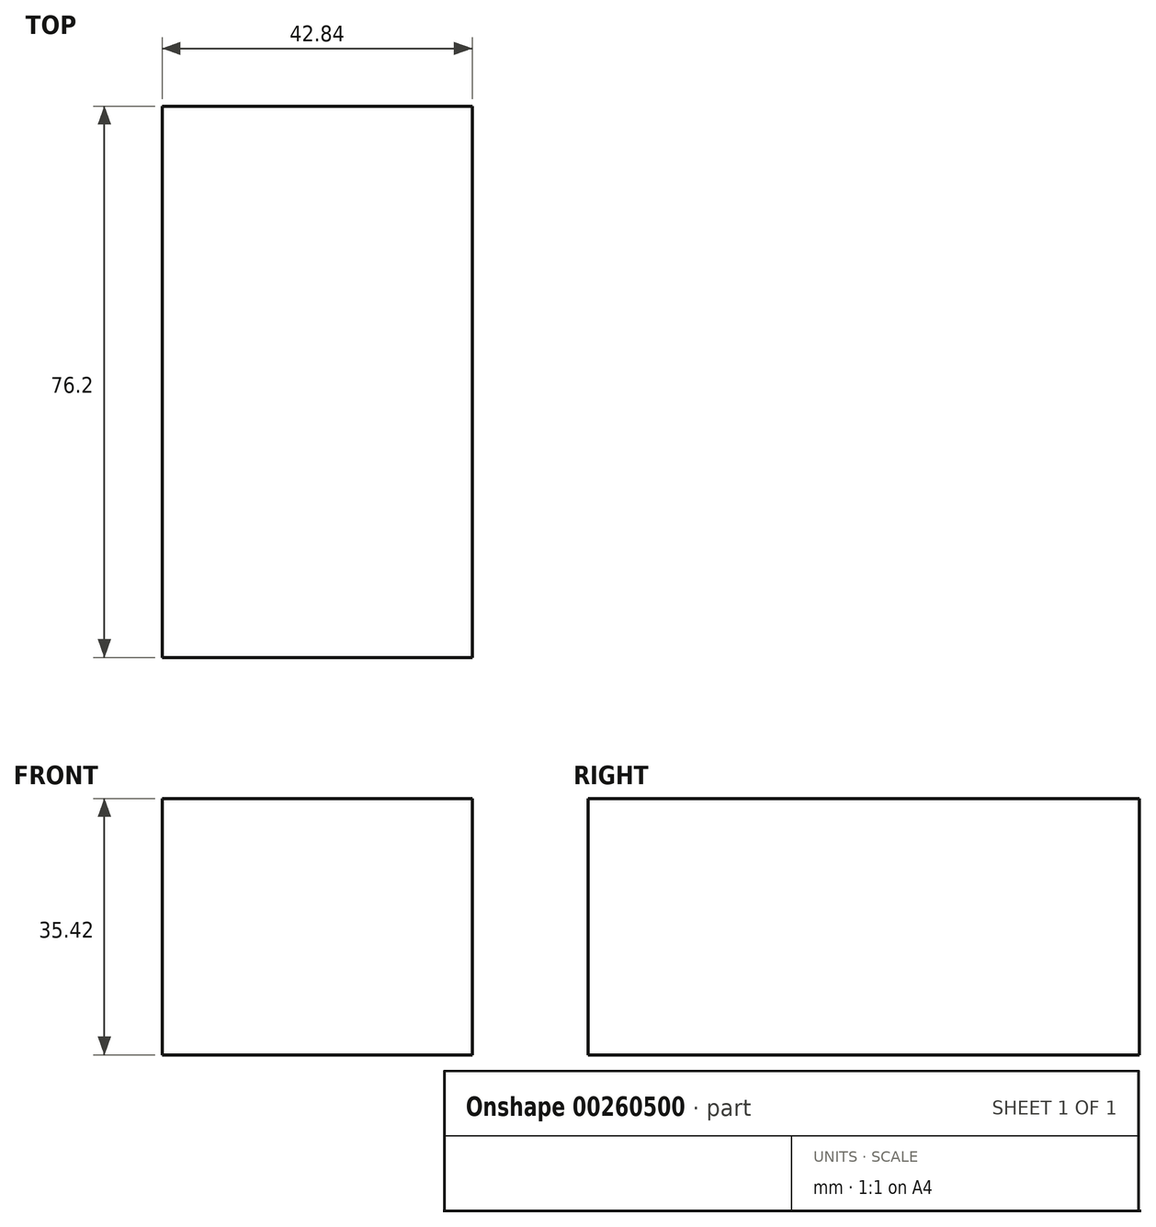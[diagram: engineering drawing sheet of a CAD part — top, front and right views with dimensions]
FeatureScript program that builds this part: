
annotation { "Feature Type Name" : "Feature", "Feature Type Description" : "" }
export const myFeature = defineFeature(function(context is Context, id is Id, definition is map)
    precondition{}
    {
        {
            var Q0;
            Q0=qCreatedBy(makeId("Front.planeOp"),FACE);
            var sketch = newSketch(context, id + "F0", { "sketchPlane" : qUnion([Q0])});
            skLineSegment(sketch, "E0.bottom", {"start": v(21.42, 17.7) * mm, "end": v(-21.42, 17.7) * mm});
            skLineSegment(sketch, "E0.top", {"start": v(21.42, -17.7) * mm, "end": v(-21.42, -17.7) * mm});
            skLineSegment(sketch, "E0.left", {"start": v(21.42, 17.7) * mm, "end": v(21.42, -17.7) * mm});
            skLineSegment(sketch, "E0.right", {"start": v(-21.42, 17.7) * mm, "end": v(-21.42, -17.7) * mm});
            skPoint(sketch, "E0.middle", {"position": v(0, 0) * mm});
            skSolve(sketch);
        }
        {
            var Q0;
            Q0 = qSketchRegion(id + "F0", true);
            extrude(context, id + "F1", {"entities" : qUnion([Q0]), "endBound" : BoundingType.SYMMETRIC, "depth" : 76.2 * mm});
        }
    });
